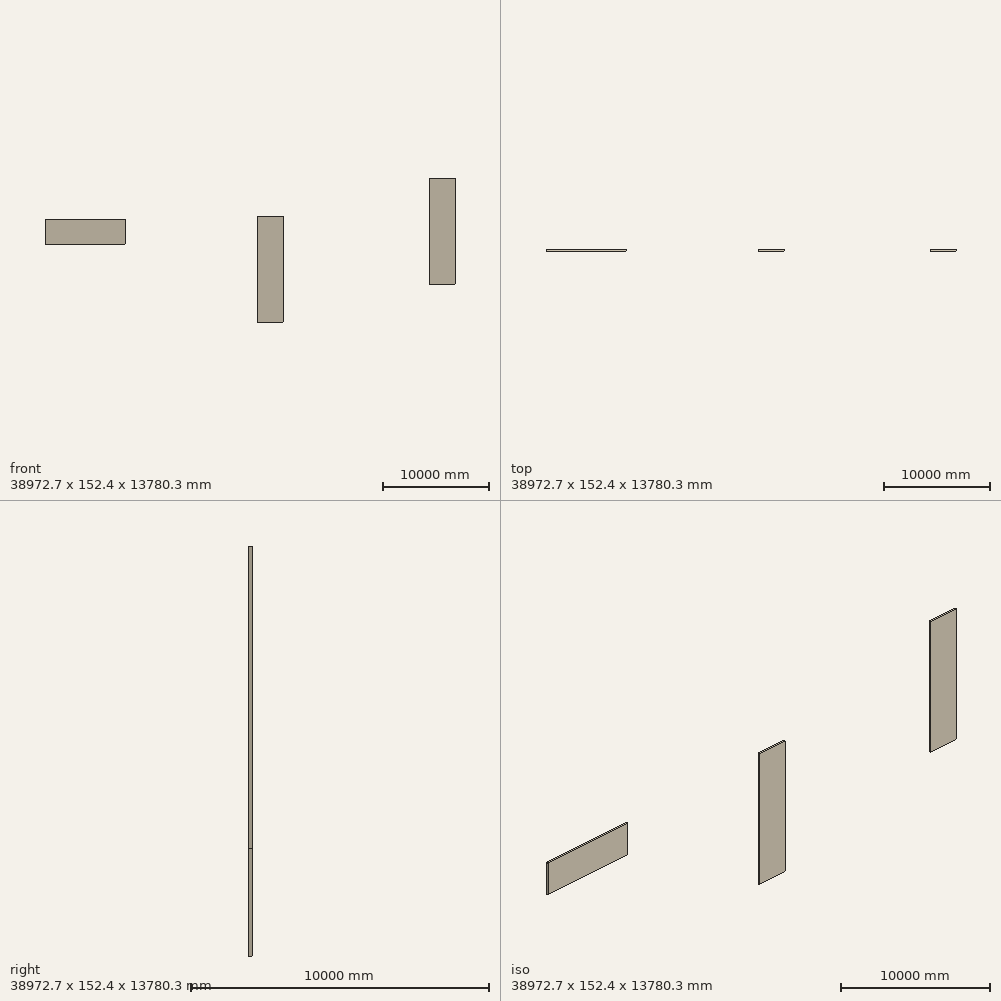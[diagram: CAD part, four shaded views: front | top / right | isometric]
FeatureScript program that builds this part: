
annotation { "Feature Type Name" : "Feature", "Feature Type Description" : "" }
export const myFeature = defineFeature(function(context is Context, id is Id, definition is map)
    precondition{}
    {
        {
            var Q0;
            Q0=qCreatedBy(makeId("Front.planeOp"),FACE);
            var sketch = newSketch(context, id + "F0", { "sketchPlane" : qUnion([Q0])});
            skLineSegment(sketch, "E0.bottom", {"start": v(-1266.63, 8979.37) * mm, "end": v(1171.77, 8979.37) * mm});
            skLineSegment(sketch, "E0.top", {"start": v(-1266.63, -1180.63) * mm, "end": v(1171.77, -1180.63) * mm});
            skLineSegment(sketch, "E0.left", {"start": v(-1266.63, 8979.37) * mm, "end": v(-1266.63, -1180.63) * mm});
            skLineSegment(sketch, "E0.right", {"start": v(1171.77, 8979.37) * mm, "end": v(1171.77, -1180.63) * mm});
            skPoint(sketch, "E0.middle", {"position": v(-47.43, 3899.37) * mm});
            skLineSegment(sketch, "E1.bottom", {"start": v(15083.32, 2439.67) * mm, "end": v(17521.72, 2439.67) * mm});
            skLineSegment(sketch, "E1.top", {"start": v(15083.32, 12599.67) * mm, "end": v(17521.72, 12599.67) * mm});
            skLineSegment(sketch, "E1.left", {"start": v(15083.32, 2439.67) * mm, "end": v(15083.32, 12599.67) * mm});
            skLineSegment(sketch, "E1.right", {"start": v(17521.72, 2439.67) * mm, "end": v(17521.72, 12599.67) * mm});
            skPoint(sketch, "E1.middle", {"position": v(16302.52, 7519.67) * mm});
            skLineSegment(sketch, "E2.bottom", {"start": v(-13830.98, 6260.72) * mm, "end": v(-21450.98, 6260.72) * mm});
            skLineSegment(sketch, "E2.top", {"start": v(-13830.98, 8699.12) * mm, "end": v(-21450.98, 8699.12) * mm});
            skLineSegment(sketch, "E2.left", {"start": v(-13830.98, 6260.72) * mm, "end": v(-13830.98, 8699.12) * mm});
            skLineSegment(sketch, "E2.right", {"start": v(-21450.98, 6260.72) * mm, "end": v(-21450.98, 8699.12) * mm});
            skPoint(sketch, "E2.middle", {"position": v(-17640.98, 7479.92) * mm});
            skSolve(sketch);
        }
        {
            var Q0;
            Q0=makeQuery(id+"F0.imprint","IMPRINT",FACE,{"disambiguationData":[TD([[makeQuery(id+"F0.imprint","IMPRINT",EDGE,{"derivedFrom":sQuery(id+"F0.wireOp",EDGE,"E2.bottom")}),-1.0]])]});
            var Q1;
            Q1=makeQuery(id+"F0.imprint","IMPRINT",FACE,{"disambiguationData":[TD([[makeQuery(id+"F0.imprint","IMPRINT",EDGE,{"derivedFrom":sQuery(id+"F0.wireOp",EDGE,"E0.bottom")}),-1.0]])]});
            var Q2;
            Q2=makeQuery(id+"F0.imprint","IMPRINT",FACE,{"disambiguationData":[TD([[makeQuery(id+"F0.imprint","IMPRINT",EDGE,{"derivedFrom":sQuery(id+"F0.wireOp",EDGE,"E1.bottom")}),1.0]])]});
            extrude(context, id + "F1", {"entities" : qUnion([Q0, Q1, Q2]), "depth" : 152.4 * mm, "offsetDistance" : 25.4 * mm});
        }
    });
